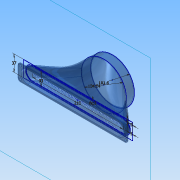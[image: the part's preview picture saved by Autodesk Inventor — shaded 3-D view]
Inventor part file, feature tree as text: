
AUTODESK INVENTOR PART (.ipt)
format: ipt  version: 2014 SP2 (Build 180246200, 246)  size: 465,920 bytes
history: native  units: mm
features: plane x4, sketch x3, loft x2, fillet x2, extrude x2, mirror x2, shell x1, hole x1
ambient origin geometry x8: Origin, YZ Plane, XZ Plane, XY Plane, X Axis, Y Axis, Z Axis, Center Point
bodies: Solid1 (feature_tree)
feature tree (17):
  sketch  "Sketch1"  dims[d1=37.0mm d2=33.0mm]
  plane  "Work Plane1"
  plane  "Work Plane2"
  sketch  "Sketch2"  dims[d3=5.0mm d4=5.0mm d5=5.0mm d6=60.0mm]
  sketch  "Sketch3"  dims[d7=104.14mm d10=0.0mm d11=90.0deg d12=20.0mm d13=101.6mm d22=0.0mm d23=90.0deg d30=0.0mm d31=90.0deg d32=0.0mm d33=90.0deg d35=2.0mm d36=2.0mm d37=0.0mm d38=2.0mm d43=4.4mm d44=6.0mm d45=4.0mm d46=2.0mm d47=90.0deg d48=8.0mm d49=20.594885mm d50=210.0mm d51=10.0mm d52=0.0mm d53=0.0mm d54=2.0mm d55=5.0mm]
  loft  "Loft1"
  loft  "Loft2"
  shell  "Shell1"  Thickness=5.0mm
  fillet  "Fillet1"  Radius=60.0mm
  extrude  "Extrusion2"  Depth=5.0mm TaperAngle=0.0deg
  plane  "Work Plane4"
  extrude  "Extrusion1"  Depth=5.0mm
  hole  "Hole1"  [1 undecoded]
  mirror  "Mirror1"
  mirror  "Mirror2"
  fillet  "Fillet2"  [1 undecoded]
  plane  "Work Plane3"
note: 2 required parameter values undecoded (feature->parameter linkage not recoverable at this tier; creation-order binding heuristic only, values carry confidence <= 0.55)
